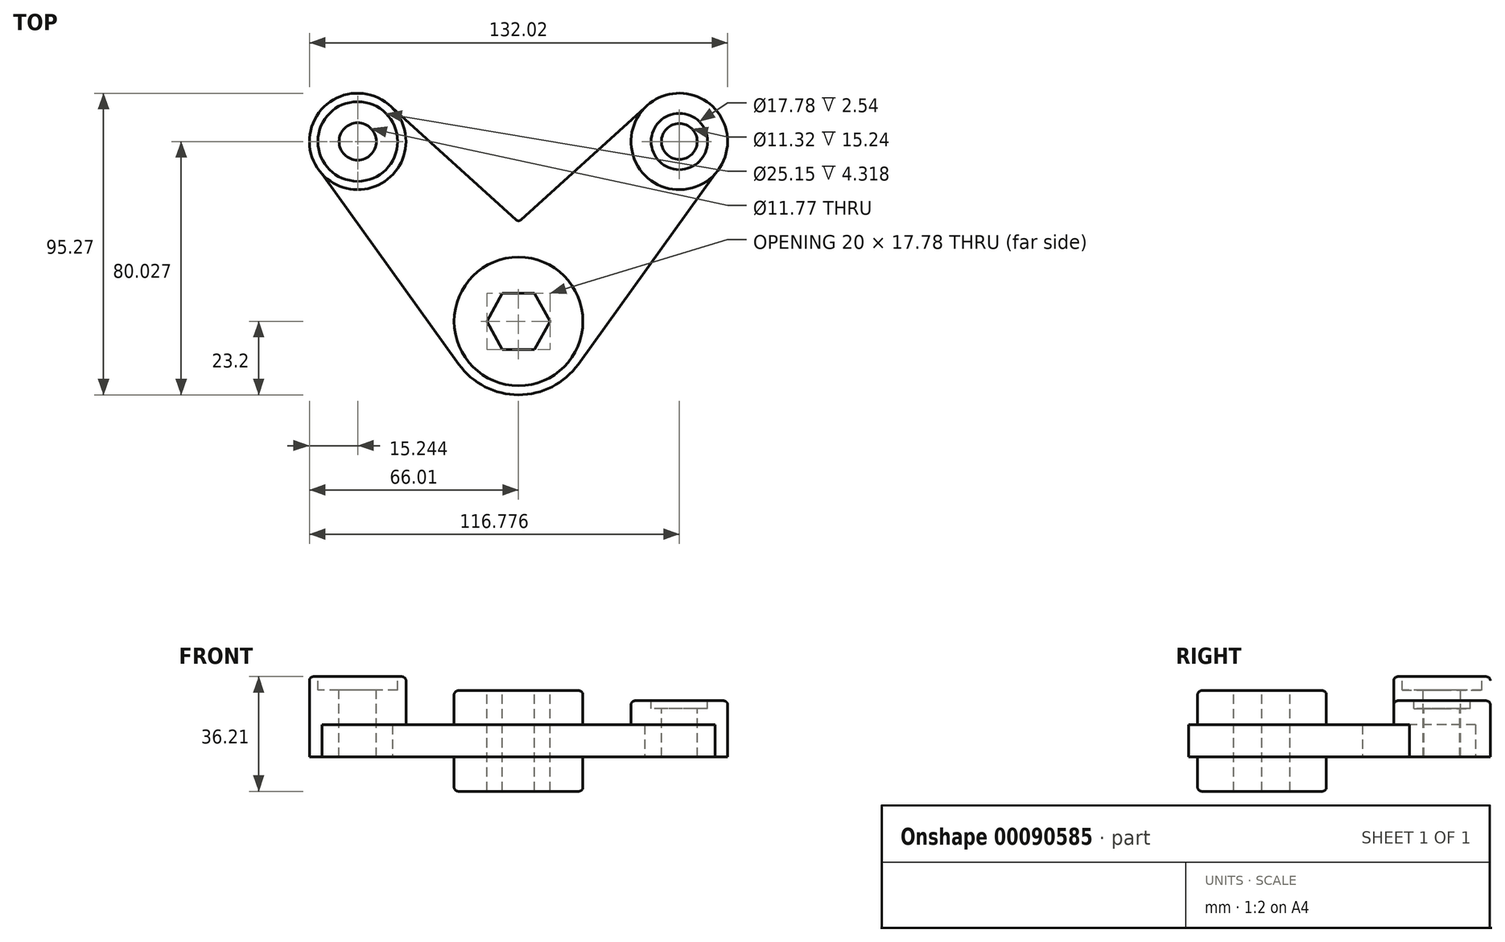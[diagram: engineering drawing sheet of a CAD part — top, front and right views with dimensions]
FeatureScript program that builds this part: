
annotation { "Feature Type Name" : "Feature", "Feature Type Description" : "" }
export const myFeature = defineFeature(function(context is Context, id is Id, definition is map)
    precondition{}
    {
        {
            var Q0;
            Q0=qCreatedBy(makeId("Top.planeOp"),FACE);
            var sketch = newSketch(context, id + "F0", { "sketchPlane" : qUnion([Q0])});
            skArc(sketch, "E0", {"start": v(-39.8, 67.4) * mm, "mid": v(-61.2, 67.94) * mm, "end": v(-62.03, 46.56) * mm});
            skArc(sketch, "E1", {"start": v(-18.84, -13.54) * mm, "mid": v(0, -23.2) * mm, "end": v(18.84, -13.54) * mm});
            skLineSegment(sketch, "E2", {"start": v(-62.03, 46.56) * mm, "end": v(-18.84, -13.54) * mm});
            skLineSegment(sketch, "E3", {"start": v(-39.8, 67.4) * mm, "end": v(0, 31.32) * mm});
            skArc(sketch, "E4.MirrorC", {"start": v(39.8, 67.4) * mm, "mid": v(61.2, 67.94) * mm, "end": v(62.03, 46.56) * mm});
            skLineSegment(sketch, "E5.MirrorCS", {"start": v(62.03, 46.56) * mm, "end": v(18.84, -13.54) * mm});
            skLineSegment(sketch, "E6.MirrorCS", {"start": v(39.8, 67.4) * mm, "end": v(0, 31.32) * mm});
            skPoint(sketch, "E7.orphan", {"position": v(-15.59, 17.2) * mm});
            skPoint(sketch, "E8.orphan", {"position": v(15.59, 17.2) * mm});
            skSolve(sketch);
        }
        {
            var Q0;
            Q0=makeQuery(id+"F0.imprint","IMPRINT",FACE,{"disambiguationData":[TD([[makeQuery(id+"F0.imprint","IMPRINT",EDGE,{"derivedFrom":sQuery(id+"F0.wireOp",EDGE,"E0")}),1.0]])]});
            extrude(context, id + "F1", {"entities" : qUnion([Q0]), "depth" : 10.16 * mm});
        }
        {
            var Q0;
            Q0=makeQuery(id+"F1.opExtrude","CAP_FACE",FACE,{"disambiguationData":[OSD([sQuery(id+"F0.wireOp",EDGE,"E0"),sQuery(id+"F0.wireOp",EDGE,"E1"),sQuery(id+"F0.wireOp",EDGE,"E2"),sQuery(id+"F0.wireOp",EDGE,"E3"),sQuery(id+"F0.wireOp",EDGE,"E4.MirrorC"),sQuery(id+"F0.wireOp",EDGE,"E5.MirrorCS"),sQuery(id+"F0.wireOp",EDGE,"E6.MirrorCS")])],"isStart":false});
            var sketch = newSketch(context, id + "F2", { "sketchPlane" : qUnion([Q0])});
            skCircle(sketch, "E9", {"center": v(50.77, 56.83) * mm, "radius": 15.24 * mm});
            skSolve(sketch);
        }
        {
            var Q0;
            Q0 = qSketchRegion(id + "F2", true);
            extrude(context, id + "F3", {"entities" : qUnion([Q0]), "operationType" : NewBodyOperationType.ADD, "depth" : 7.62 * mm});
        }
        {
            var Q0;
            Q0=makeQuery(id+"F3.opExtrude","CAP_EDGE",EDGE,{"disambiguationData":[OSD([sQuery(id+"F2.wireOp",EDGE,"E9")])],"isStart":false});
            fillet(context, id + "F4", {"entities" : qUnion([Q0]), "radius" : 1.27 * mm, "tangentPropagation" : true, "allowEdgeOverflow" : false});
        }
        {
            var Q0;
            Q0=makeQuery(id+"F3.opExtrude","CAP_FACE",FACE,{"disambiguationData":[OSD([sQuery(id+"F2.wireOp",EDGE,"E9")])],"isStart":false});
            var sketch = newSketch(context, id + "F5", { "sketchPlane" : qUnion([Q0])});
            skCircle(sketch, "E10", {"center": v(50.77, 56.83) * mm, "radius": 8.9 * mm});
            skSolve(sketch);
        }
        {
            var Q0;
            Q0=makeQuery(id+"F5.imprint","IMPRINT",FACE,{"disambiguationData":[TD([[makeQuery(id+"F5.imprint","IMPRINT",EDGE,{"derivedFrom":sQuery(id+"F5.wireOp",EDGE,"E10")}),1.0]])]});
            extrude(context, id + "F6", {"entities" : qUnion([Q0]), "operationType" : NewBodyOperationType.REMOVE, "oppositeDirection" : true, "depth" : 2.54 * mm, "hasSecondDirection" : true, "secondDirectionOppositeDirection" : false, "secondDirectionDepth" : 25.4 * mm});
        }
        {
            var Q0;
            Q0=makeQuery(id+"F6.boolean.opBoolean","COPY",FACE,{"derivedFrom":makeQuery(id+"F6.opExtrude","CAP_FACE",FACE,{"disambiguationData":[OSD([sQuery(id+"F5.wireOp",EDGE,"E10")])],"isStart":false})});
            var sketch = newSketch(context, id + "F7", { "sketchPlane" : qUnion([Q0])});
            skCircle(sketch, "E11", {"center": v(50.77, 56.83) * mm, "radius": 5.66 * mm});
            skSolve(sketch);
        }
        {
            var Q0;
            Q0=makeQuery(id+"F7.imprint","IMPRINT",FACE,{"disambiguationData":[TD([[makeQuery(id+"F7.imprint","IMPRINT",EDGE,{"derivedFrom":sQuery(id+"F7.wireOp",EDGE,"E11")}),1.0]])]});
            extrude(context, id + "F8", {"entities" : qUnion([Q0]), "operationType" : NewBodyOperationType.REMOVE, "endBound" : BoundingType.THROUGH_ALL, "oppositeDirection" : true, "depth" : 25.4 * mm});
        }
        {
            var Q0;
            Q0=makeQuery(id+"F1.opExtrude","SWEPT_EDGE",EDGE,{"disambiguationData":[OSD([sQuery(id+"F0.wireOp",EDGE,"E3"),sQuery(id+"F0.wireOp",EDGE,"E6.MirrorCS")])]});
            fillet(context, id + "F9", {"entities" : qUnion([Q0]), "radius" : 1.27 * mm, "tangentPropagation" : true, "allowEdgeOverflow" : false});
        }
        {
            var Q0;
            Q0=makeQuery(id+"F1.opExtrude","CAP_FACE",FACE,{"disambiguationData":[OSD([sQuery(id+"F0.wireOp",EDGE,"E0"),sQuery(id+"F0.wireOp",EDGE,"E1"),sQuery(id+"F0.wireOp",EDGE,"E2"),sQuery(id+"F0.wireOp",EDGE,"E3"),sQuery(id+"F0.wireOp",EDGE,"E4.MirrorC"),sQuery(id+"F0.wireOp",EDGE,"E5.MirrorCS"),sQuery(id+"F0.wireOp",EDGE,"E6.MirrorCS")])],"isStart":false});
            var sketch = newSketch(context, id + "F10", { "sketchPlane" : qUnion([Q0])});
            skCircle(sketch, "E12", {"center": v(-50.77, 56.83) * mm, "radius": 15.24 * mm});
            skSolve(sketch);
        }
        {
            var Q0;
            {var subQ0=sQuery(id+"F10.wireOp",EDGE,"E12");var subQ1=makeQuery(id+"F10.imprint","INTERSECT",VERTEX,{"derivedFrom":[makeQuery(id+"F1.opExtrude","CAP_EDGE",EDGE,{"disambiguationData":[OSD([sQuery(id+"F0.wireOp",EDGE,"E3")])],"isStart":false}),subQ0]});Q0=makeQuery(id+"F10.imprint","IMPRINT",FACE,{"disambiguationData":[TD([[makeQuery(id+"F10.imprint","IMPRINT",EDGE,{"disambiguationData":[TD([[subQ1,-1.0]])],"derivedFrom":subQ0}),1.0]])]});}
            extrude(context, id + "F11", {"entities" : qUnion([Q0]), "operationType" : NewBodyOperationType.ADD, "depth" : 15.24 * mm});
        }
        {
            var Q0;
            Q0=makeQuery(id+"F11.opExtrude","CAP_EDGE",EDGE,{"disambiguationData":[OSD([sQuery(id+"F10.wireOp",EDGE,"E12")])],"isStart":false});
            fillet(context, id + "F12", {"entities" : qUnion([Q0]), "radius" : 1.27 * mm, "tangentPropagation" : true, "allowEdgeOverflow" : false});
        }
        {
            var Q0;
            Q0=makeQuery(id+"F11.opExtrude","CAP_FACE",FACE,{"disambiguationData":[OSD([sQuery(id+"F10.wireOp",EDGE,"E12")])],"isStart":false});
            var sketch = newSketch(context, id + "F13", { "sketchPlane" : qUnion([Q0])});
            skCircle(sketch, "E13", {"center": v(-50.77, 56.83) * mm, "radius": 12.57 * mm});
            skSolve(sketch);
        }
        {
            var Q0;
            Q0=makeQuery(id+"F13.imprint","IMPRINT",FACE,{"disambiguationData":[TD([[makeQuery(id+"F13.imprint","IMPRINT",EDGE,{"derivedFrom":sQuery(id+"F13.wireOp",EDGE,"E13")}),1.0]])]});
            extrude(context, id + "F14", {"entities" : qUnion([Q0]), "operationType" : NewBodyOperationType.REMOVE, "oppositeDirection" : true, "depth" : 4.32 * mm});
        }
        {
            var Q0;
            Q0=makeQuery(id+"F14.boolean.opBoolean","COPY",FACE,{"derivedFrom":makeQuery(id+"F14.opExtrude","CAP_FACE",FACE,{"disambiguationData":[OSD([sQuery(id+"F13.wireOp",EDGE,"E13")])],"isStart":false})});
            var sketch = newSketch(context, id + "F15", { "sketchPlane" : qUnion([Q0])});
            skCircle(sketch, "E14", {"center": v(-50.77, 56.83) * mm, "radius": 5.88 * mm});
            skSolve(sketch);
        }
        {
            var Q0;
            Q0=makeQuery(id+"F15.imprint","IMPRINT",FACE,{"disambiguationData":[TD([[makeQuery(id+"F15.imprint","IMPRINT",EDGE,{"derivedFrom":sQuery(id+"F15.wireOp",EDGE,"E14")}),1.0]])]});
            extrude(context, id + "F16", {"entities" : qUnion([Q0]), "operationType" : NewBodyOperationType.REMOVE, "endBound" : BoundingType.THROUGH_ALL, "oppositeDirection" : true, "depth" : 25.4 * mm});
        }
        {
            var Q0;
            Q0=makeQuery(id+"F1.opExtrude","CAP_FACE",FACE,{"disambiguationData":[OSD([sQuery(id+"F0.wireOp",EDGE,"E0"),sQuery(id+"F0.wireOp",EDGE,"E1"),sQuery(id+"F0.wireOp",EDGE,"E2"),sQuery(id+"F0.wireOp",EDGE,"E3"),sQuery(id+"F0.wireOp",EDGE,"E4.MirrorC"),sQuery(id+"F0.wireOp",EDGE,"E5.MirrorCS"),sQuery(id+"F0.wireOp",EDGE,"E6.MirrorCS")])],"isStart":false});
            var sketch = newSketch(context, id + "F17", { "sketchPlane" : qUnion([Q0])});
            skCircle(sketch, "E15", {"center": v(0, 0) * mm, "radius": 20.32 * mm});
            skSolve(sketch);
        }
        {
            var Q0;
            Q0=makeQuery(id+"F17.imprint","IMPRINT",FACE,{"disambiguationData":[TD([[makeQuery(id+"F17.imprint","IMPRINT",EDGE,{"derivedFrom":sQuery(id+"F17.wireOp",EDGE,"E15")}),1.0]])]});
            extrude(context, id + "F18", {"entities" : qUnion([Q0]), "operationType" : NewBodyOperationType.ADD, "depth" : 10.8 * mm});
        }
        {
            var Q0;
            Q0=makeQuery(id+"F18.opExtrude","CAP_FACE",FACE,{"disambiguationData":[OSD([sQuery(id+"F17.wireOp",EDGE,"E15")])],"isStart":false});
            var sketch = newSketch(context, id + "F19", { "sketchPlane" : qUnion([Q0])});
            skLineSegment(sketch, "E16.bottom", {"start": v(-5.08, 8.9) * mm, "end": v(5.08, 8.9) * mm});
            skLineSegment(sketch, "E16.top", {"start": v(-5.08, -8.9) * mm, "end": v(5.08, -8.9) * mm});
            skPoint(sketch, "E16.middle", {"position": v(0, 0) * mm});
            skLineSegment(sketch, "E17", {"start": v(-5.08, 8.9) * mm, "end": v(-10, 0) * mm});
            skPoint(sketch, "E17.endSnap0", {"position": v(-5.08, 0) * mm});
            skLineSegment(sketch, "E18", {"start": v(-10, 0) * mm, "end": v(-5.08, -8.9) * mm});
            skLineSegment(sketch, "E19.MirrorCS", {"start": v(5.08, 8.9) * mm, "end": v(10, 0) * mm});
            skLineSegment(sketch, "E20.MirrorCS", {"start": v(10, 0) * mm, "end": v(5.08, -8.9) * mm});
            skSolve(sketch);
        }
        {
            var Q0;
            Q0=makeQuery(id+"F19.imprint","IMPRINT",FACE,{"disambiguationData":[TD([[makeQuery(id+"F19.imprint","IMPRINT",EDGE,{"derivedFrom":sQuery(id+"F19.wireOp",EDGE,"E16.bottom")}),-1.0]])]});
            extrude(context, id + "F20", {"entities" : qUnion([Q0]), "operationType" : NewBodyOperationType.REMOVE, "oppositeDirection" : true, "depth" : 25.4 * mm});
        }
        {
            var Q0;
            Q0=makeQuery(id+"F1.opExtrude","CAP_FACE",FACE,{"disambiguationData":[OSD([sQuery(id+"F0.wireOp",EDGE,"E0"),sQuery(id+"F0.wireOp",EDGE,"E1"),sQuery(id+"F0.wireOp",EDGE,"E2"),sQuery(id+"F0.wireOp",EDGE,"E3"),sQuery(id+"F0.wireOp",EDGE,"E4.MirrorC"),sQuery(id+"F0.wireOp",EDGE,"E5.MirrorCS"),sQuery(id+"F0.wireOp",EDGE,"E6.MirrorCS")])],"isStart":true});
            var sketch = newSketch(context, id + "F21", { "sketchPlane" : qUnion([Q0])});
            skCircle(sketch, "E21", {"center": v(0, 0) * mm, "radius": 20.32 * mm});
            skSolve(sketch);
        }
        {
            var Q0;
            Q0=makeQuery(id+"F21.imprint","IMPRINT",FACE,{"disambiguationData":[TD([[makeQuery(id+"F21.imprint","IMPRINT",EDGE,{"derivedFrom":sQuery(id+"F21.wireOp",EDGE,"E21")}),1.0]])]});
            var Q1;
            Q1=makeQuery(id+"F3.opExtrude","CAP_FACE",FACE,{"disambiguationData":[OSD([sQuery(id+"F2.wireOp",EDGE,"E9")])],"isStart":false});
            extrude(context, id + "F22", {"entities" : qUnion([Q0, Q1]), "operationType" : NewBodyOperationType.ADD, "depth" : 10.8 * mm});
        }
        {
            var Q0;
            Q0=makeQuery(id+"F18.opExtrude","CAP_EDGE",EDGE,{"disambiguationData":[OSD([sQuery(id+"F17.wireOp",EDGE,"E15")])],"isStart":false});
            var Q1;
            Q1=makeQuery(id+"F22.opExtrude","CAP_EDGE",EDGE,{"disambiguationData":[OSD([sQuery(id+"F21.wireOp",EDGE,"E21")])],"isStart":false});
            fillet(context, id + "F23", {"entities" : qUnion([Q0, Q1]), "radius" : 1.27 * mm, "tangentPropagation" : true, "allowEdgeOverflow" : false});
        }
    });
